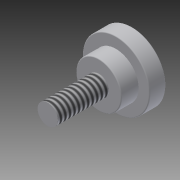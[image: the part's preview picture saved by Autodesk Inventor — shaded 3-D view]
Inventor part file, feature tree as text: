
AUTODESK INVENTOR PART (.ipt)
format: ipt  version: 2014 (Build 180170000, 170)  size: 119,808 bytes
history: native  units: in
note: dims shown in document units (in); Inventor stores cm internally (conversion verified against a paired STEP export)
features: extrude x3, fillet x3, sketch x3, thread x1
ambient origin geometry x8: Origin, YZ Plane, XZ Plane, XY Plane, X Axis, Y Axis, Z Axis, Center Point
bodies: Solid1 (feature_tree)
feature tree (10):
  extrude  "Extrusion1"  Depth=0.09in
  extrude  "Extrusion2"  Depth=0.095in
  extrude  "Extrusion3"  Depth=0.005in TaperAngle=0.0deg
  thread  "Thread1"  [1 undecoded]
  fillet  "Fillet1"  Radius=0.005in
  fillet  "Fillet2"  Radius=0.005in
  fillet  "Fillet3"  [1 undecoded]
  sketch  "Sketch1"  dims[d3=0.09in d4=0.0in d5=0.25in]
  sketch  "Sketch2"  dims[d6=0.095in d7=0.0in d8=0.112in]
  sketch  "Sketch3"  dims[d9=0.28in d10=0.0in d11=1.0in d12=0.0in d13=0.005in d14=0.005in d15=0.005in]
note: 2 required parameter values undecoded (feature->parameter linkage not recoverable at this tier; creation-order binding heuristic only, values carry confidence <= 0.55)
